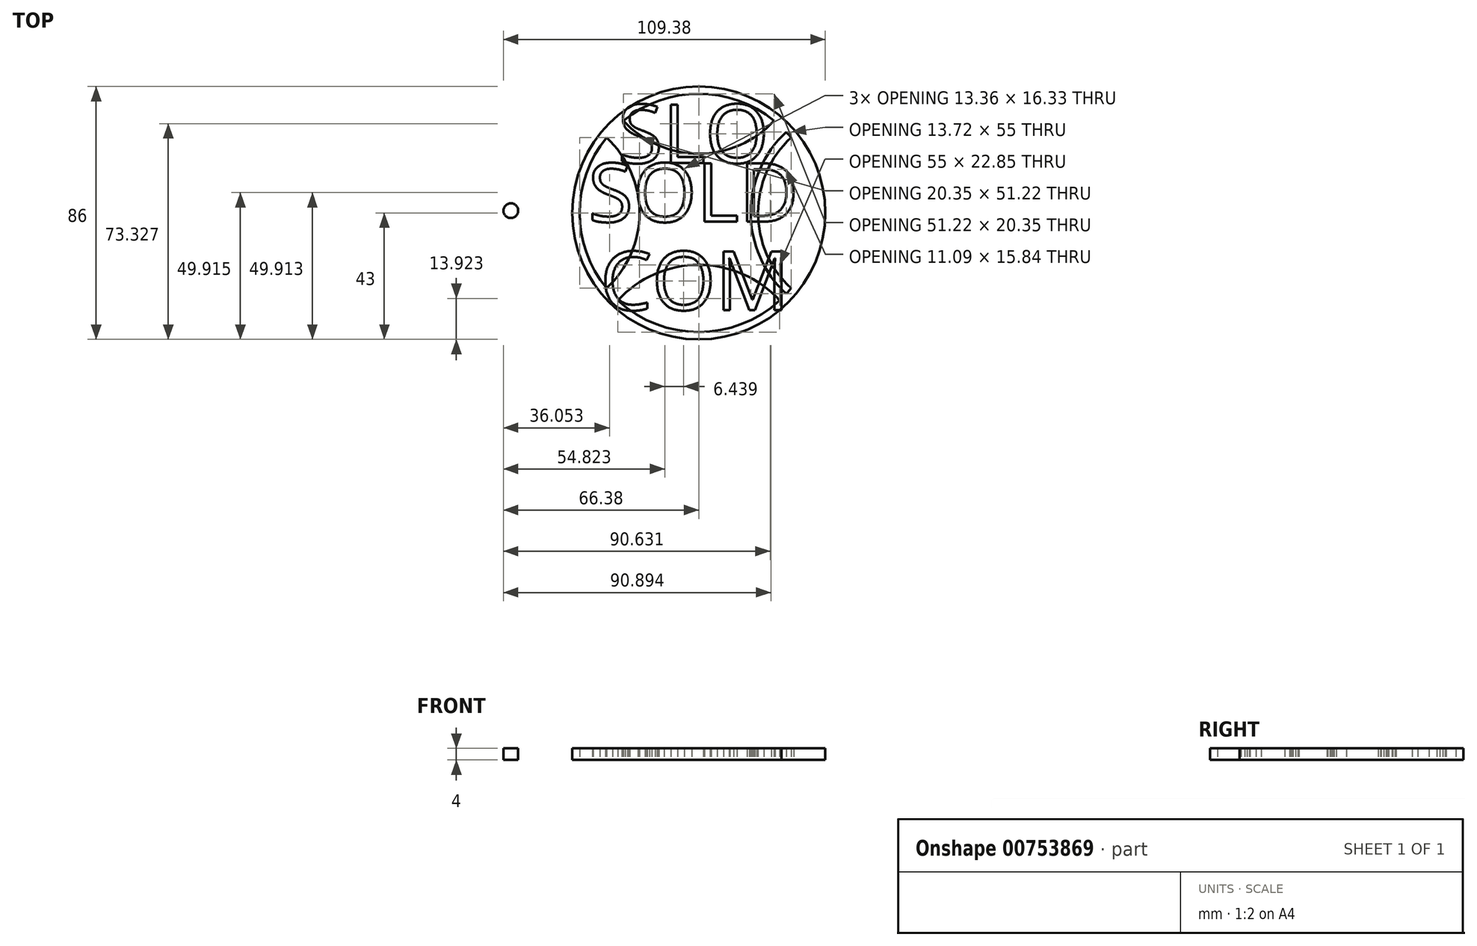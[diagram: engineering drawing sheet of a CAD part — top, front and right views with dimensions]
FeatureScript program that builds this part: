
annotation { "Feature Type Name" : "Feature", "Feature Type Description" : "" }
export const myFeature = defineFeature(function(context is Context, id is Id, definition is map)
    precondition{}
    {
        {
            var Q0;
            Q0=qCreatedBy(makeId("Top.planeOp"),FACE);
            var sketch = newSketch(context, id + "F0", { "sketchPlane" : qUnion([Q0])});
            skText(sketch, "E0", { "text": "SOLD", "fontName": "OpenSans-Regular.ttf"});
            skText(sketch, "E1", { "text": "SLO", "fontName": "OpenSans-Regular.ttf"});
            skText(sketch, "E2", { "text": "COM", "fontName": "OpenSans-Regular.ttf"});
            const initialGuessF0  = {"E0": [-0.02462, 0.01, 1, 0, 0.02], "E1": [-0.0145, 0.03, 1, 0, 0.02], "E2": [-0.02046, -0.02, 1, 0, 0.02]};
            skSetInitialGuess(sketch, initialGuessF0);
            skSolve(sketch);
        }
        {
            var Q0;
            Q0 = qSketchRegion(id + "F0", true);
            extrude(context, id + "F1", {"entities" : qUnion([Q0]), "depth" : 4 * mm, "offsetDistance" : 25.4 * mm});
        }
        {
            var Q0;
            Q0=qCreatedBy(makeId("Top.planeOp"),FACE);
            var sketch = newSketch(context, id + "F2", { "sketchPlane" : qUnion([Q0])});
            skCircle(sketch, "E3", {"center": v(13, 13) * mm, "radius": 40.5 * mm});
            skCircle(sketch, "E4", {"center": v(13, 13) * mm, "radius": 43 * mm});
            skCircle(sketch, "E5", {"center": v(-50.88, 13.77) * mm, "radius": 2.5 * mm});
            skLineSegment(sketch, "E6", {"start": v(-27.5, 13) * mm, "end": v(53.5, 13) * mm, "construction": true});
            skLineSegment(sketch, "E7", {"start": v(13, 53.5) * mm, "end": v(13, -27.5) * mm, "construction": true});
            skArc(sketch, "E8", {"start": v(-12.61, 44.37) * mm, "mid": v(13, 33.15) * mm, "end": v(38.61, 44.37) * mm});
            skArc(sketch, "E9", {"start": v(-14.5, 42.73) * mm, "mid": v(13, 30.65) * mm, "end": v(40.5, 42.73) * mm});
            skLineSegment(sketch, "E10", {"start": v(41.64, 41.64) * mm, "end": v(-15.64, -15.64) * mm, "construction": true});
            skArc(sketch, "E11.MirrorCS", {"start": v(-14.5, -16.73) * mm, "mid": v(13, -4.65) * mm, "end": v(40.5, -16.73) * mm});
            skArc(sketch, "E12.MirrorCS", {"start": v(-12.61, -18.37) * mm, "mid": v(13, -7.15) * mm, "end": v(38.61, -18.37) * mm});
            skLineSegment(sketch, "E13.MirrorCS", {"start": v(53.5, 13) * mm, "end": v(-27.5, 13) * mm, "construction": true});
            skArc(sketch, "E14.MirrorCS", {"start": v(44.37, -12.61) * mm, "mid": v(33.15, 13) * mm, "end": v(44.37, 38.61) * mm});
            skArc(sketch, "E15.MirrorCS", {"start": v(42.73, -14.5) * mm, "mid": v(30.65, 13) * mm, "end": v(42.73, 40.5) * mm});
            skArc(sketch, "E16.MirrorCS", {"start": v(-16.73, -14.5) * mm, "mid": v(-4.65, 13) * mm, "end": v(-16.73, 40.5) * mm});
            skArc(sketch, "E17.MirrorCS", {"start": v(-18.37, -12.61) * mm, "mid": v(-7.15, 13) * mm, "end": v(-18.37, 38.61) * mm});
            skSolve(sketch);
        }
        {
            var Q0;
            Q0=makeQuery(id+"F2.imprint","IMPRINT",FACE,{"disambiguationData":[TD([[makeQuery(id+"F2.imprint","IMPRINT",EDGE,{"derivedFrom":sQuery(id+"F2.wireOp",EDGE,"E3")}),-1.0]])]});
            var Q1;
            Q1=makeQuery(id+"F2.imprint","IMPRINT",FACE,{"disambiguationData":[TD([[makeQuery(id+"F2.imprint","IMPRINT",EDGE,{"derivedFrom":sQuery(id+"F2.wireOp",EDGE,"E5")}),1.0]])]});
            var Q2;
            {var subQ0=sQuery(id+"F2.wireOp",EDGE,"E16.MirrorCS");Q2=makeQuery(id+"F2.imprint","IMPRINT",FACE,{"disambiguationData":[TD([[makeQuery(id+"F2.imprint","IMPRINT",EDGE,{"derivedFrom":subQ0}),1.0]])]});}
            var Q3;
            {var subQ0=sQuery(id+"F2.wireOp",EDGE,"E8");Q3=makeQuery(id+"F2.imprint","IMPRINT",FACE,{"disambiguationData":[TD([[makeQuery(id+"F2.imprint","IMPRINT",EDGE,{"derivedFrom":subQ0}),-1.0]])]});}
            var Q4;
            {var subQ0=sQuery(id+"F2.wireOp",EDGE,"E14.MirrorCS");Q4=makeQuery(id+"F2.imprint","IMPRINT",FACE,{"disambiguationData":[TD([[makeQuery(id+"F2.imprint","IMPRINT",EDGE,{"derivedFrom":subQ0}),1.0]])]});}
            var Q5;
            {var subQ0=sQuery(id+"F2.wireOp",EDGE,"E11.MirrorCS");Q5=makeQuery(id+"F2.imprint","IMPRINT",FACE,{"disambiguationData":[TD([[makeQuery(id+"F2.imprint","IMPRINT",EDGE,{"derivedFrom":subQ0}),-1.0]])]});}
            var Q6;
            Q6=makeQuery(id+"F1.opExtrude","CAP_FACE",FACE,{"disambiguationData":[OSD([sQuery(id+"F0.wireOp",EDGE,"E2.sketch_text.stroke-0"),sQuery(id+"F0.wireOp",EDGE,"E2.sketch_text.stroke-1"),sQuery(id+"F0.wireOp",EDGE,"E2.sketch_text.stroke-2"),sQuery(id+"F0.wireOp",EDGE,"E2.sketch_text.stroke-3"),sQuery(id+"F0.wireOp",EDGE,"E2.sketch_text.stroke-4"),sQuery(id+"F0.wireOp",EDGE,"E2.sketch_text.stroke-5"),sQuery(id+"F0.wireOp",EDGE,"E2.sketch_text.stroke-6"),sQuery(id+"F0.wireOp",EDGE,"E2.sketch_text.stroke-7"),sQuery(id+"F0.wireOp",EDGE,"E2.sketch_text.stroke-8"),sQuery(id+"F0.wireOp",EDGE,"E2.sketch_text.stroke-9"),sQuery(id+"F0.wireOp",EDGE,"E2.sketch_text.stroke-10"),sQuery(id+"F0.wireOp",EDGE,"E2.sketch_text.stroke-11"),sQuery(id+"F0.wireOp",EDGE,"E2.sketch_text.stroke-12"),sQuery(id+"F0.wireOp",EDGE,"E2.sketch_text.stroke-13"),sQuery(id+"F0.wireOp",EDGE,"E2.sketch_text.stroke-14")])],"isStart":false});
            extrude(context, id + "F3", {"entities" : qUnion([Q0, Q1, Q2, Q3, Q4, Q5]), "endBound" : BoundingType.UP_TO_SURFACE, "depth" : 25 * mm, "endBoundEntityFace" : qUnion([Q6]), "offsetDistance" : 25 * mm});
        }
    });
